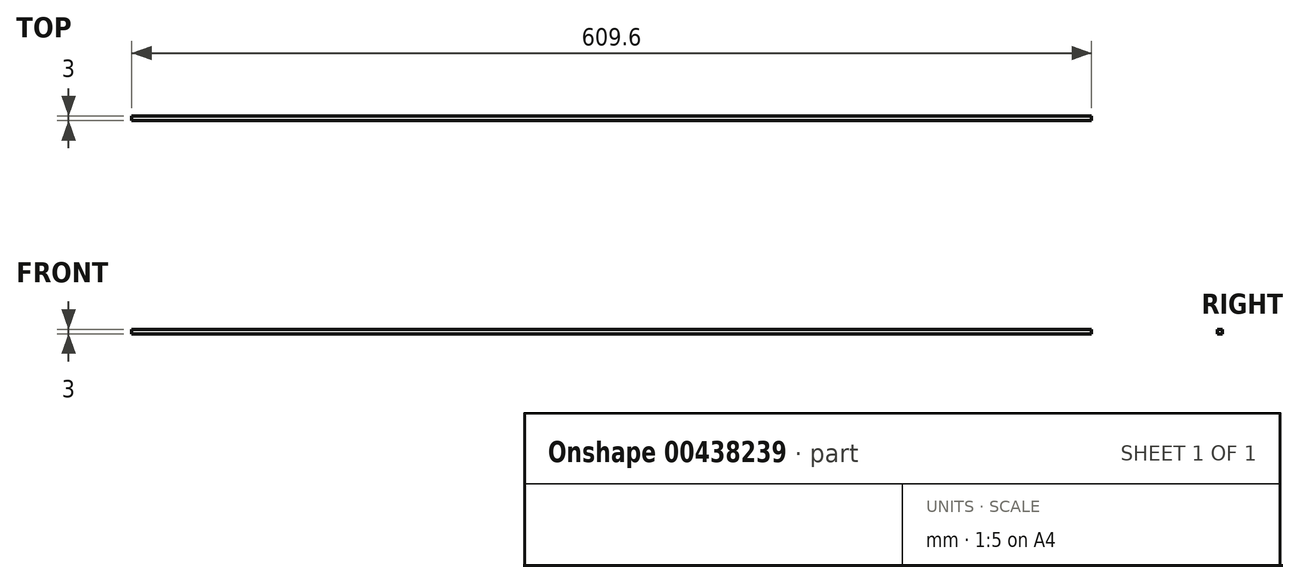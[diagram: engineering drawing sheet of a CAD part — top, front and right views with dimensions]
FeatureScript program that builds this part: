
annotation { "Feature Type Name" : "Feature", "Feature Type Description" : "" }
export const myFeature = defineFeature(function(context is Context, id is Id, definition is map)
    precondition{}
    {
        {
            var Q0;
            Q0=qCreatedBy(makeId("Front.planeOp"),FACE);
            var sketch = newSketch(context, id + "F0", { "sketchPlane" : qUnion([Q0])});
            skLineSegment(sketch, "E0.bottom", {"start": v(-280.25, 29.8) * mm, "end": v(329.35, 29.8) * mm});
            skLineSegment(sketch, "E0.top", {"start": v(-280.25, 26.8) * mm, "end": v(329.35, 26.8) * mm});
            skLineSegment(sketch, "E0.left", {"start": v(-280.25, 29.8) * mm, "end": v(-280.25, 26.8) * mm});
            skLineSegment(sketch, "E0.right", {"start": v(329.35, 29.8) * mm, "end": v(329.35, 26.8) * mm});
            skSolve(sketch);
        }
        {
            var Q0;
            Q0 = qSketchRegion(id + "F0", true);
            extrude(context, id + "F1", {"entities" : qUnion([Q0]), "oppositeDirection" : true, "depth" : 3 * mm});
        }
    });
